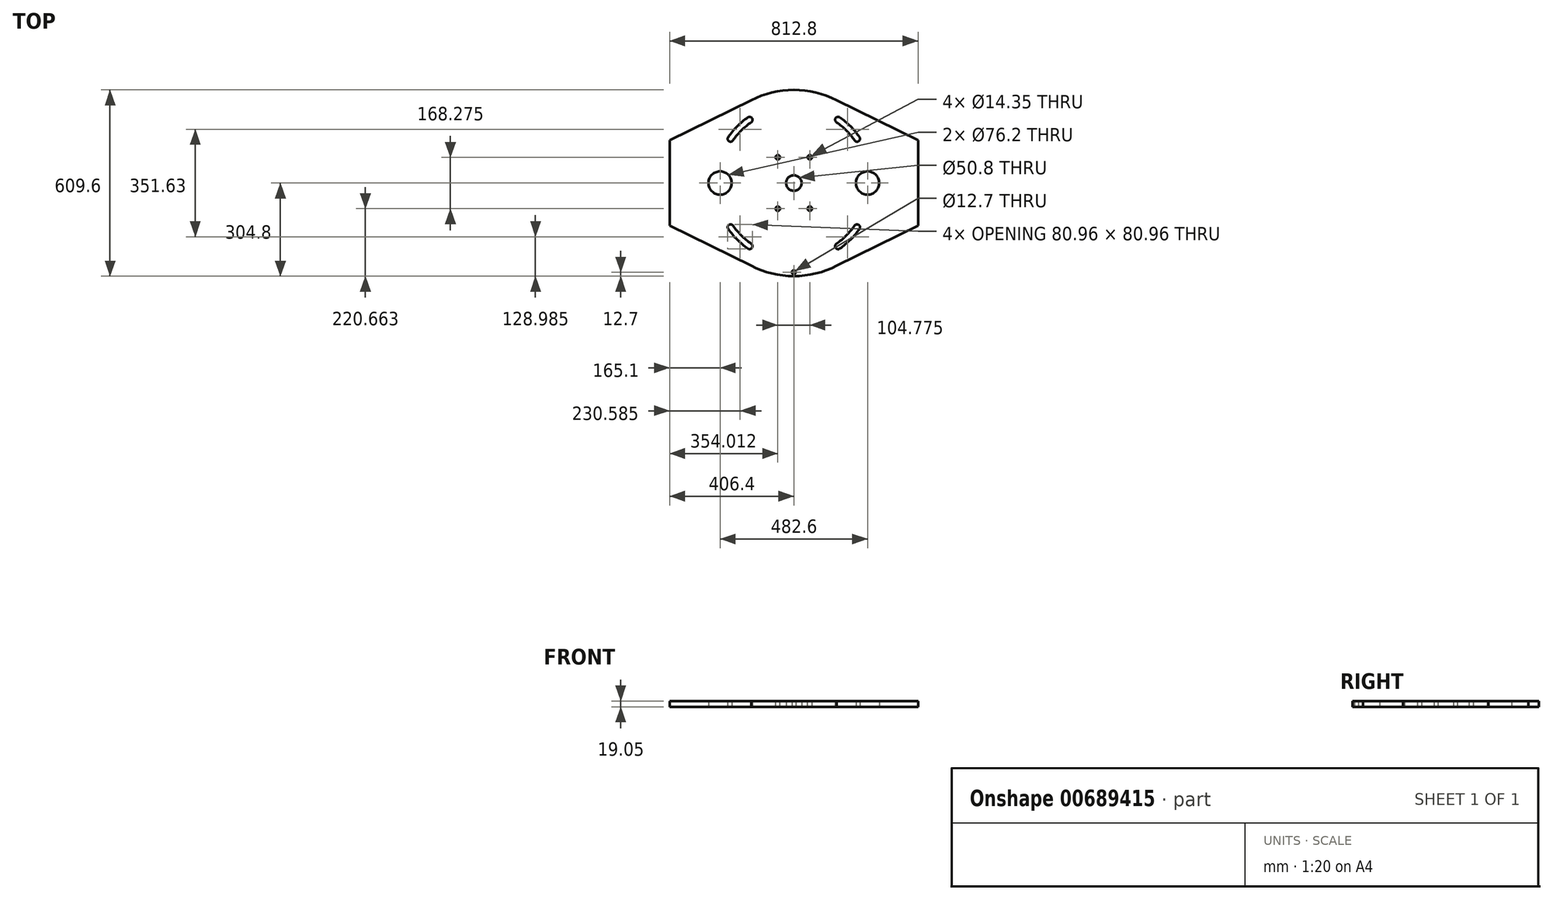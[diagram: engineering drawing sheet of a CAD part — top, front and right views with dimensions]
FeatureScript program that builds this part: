
annotation { "Feature Type Name" : "Feature", "Feature Type Description" : "" }
export const myFeature = defineFeature(function(context is Context, id is Id, definition is map)
    precondition{}
    {
        {
            var Q0;
            Q0=qCreatedBy(makeId("Top.planeOp"),FACE);
            var sketch = newSketch(context, id + "F0", { "sketchPlane" : qUnion([Q0])});
            skCircle(sketch, "E0", {"center": v(0, 0) * mm, "radius": 304.8 * mm});
            skCircle(sketch, "E1", {"center": v(0, 0) * mm, "radius": 25.4 * mm});
            skCircle(sketch, "E2", {"center": v(241.3, 0) * mm, "radius": 38.1 * mm});
            skCircle(sketch, "E3", {"center": v(-241.3, 0) * mm, "radius": 38.1 * mm});
            skArc(sketch, "E4", {"start": v(-198.93, -139.3) * mm, "mid": v(-212.34, -136.93) * mm, "end": v(-214.7, -150.34) * mm});
            skArc(sketch, "E5", {"start": v(-150.34, -214.7) * mm, "mid": v(-136.93, -212.34) * mm, "end": v(-139.3, -198.93) * mm});
            skArc(sketch, "E6", {"start": v(-198.93, -139.3) * mm, "mid": v(-171.72, -171.72) * mm, "end": v(-139.3, -198.93) * mm});
            skArc(sketch, "E7", {"start": v(-214.7, -150.34) * mm, "mid": v(-185.33, -185.33) * mm, "end": v(-150.34, -214.7) * mm});
            skArc(sketch, "E8.1.0", {"start": v(214.7, -150.34) * mm, "mid": v(212.34, -136.93) * mm, "end": v(198.93, -139.3) * mm});
            skArc(sketch, "E8.1.1", {"start": v(139.3, -198.93) * mm, "mid": v(171.72, -171.72) * mm, "end": v(198.93, -139.3) * mm});
            skArc(sketch, "E8.1.2", {"start": v(150.34, -214.7) * mm, "mid": v(185.33, -185.33) * mm, "end": v(214.7, -150.34) * mm});
            skArc(sketch, "E8.1.3", {"start": v(139.3, -198.93) * mm, "mid": v(136.93, -212.34) * mm, "end": v(150.34, -214.7) * mm});
            skArc(sketch, "E8.2.0", {"start": v(150.34, 214.7) * mm, "mid": v(136.93, 212.34) * mm, "end": v(139.3, 198.93) * mm});
            skArc(sketch, "E8.2.1", {"start": v(198.93, 139.3) * mm, "mid": v(171.72, 171.72) * mm, "end": v(139.3, 198.93) * mm});
            skArc(sketch, "E8.2.2", {"start": v(214.7, 150.34) * mm, "mid": v(185.33, 185.33) * mm, "end": v(150.34, 214.7) * mm});
            skArc(sketch, "E8.2.3", {"start": v(198.93, 139.3) * mm, "mid": v(212.34, 136.93) * mm, "end": v(214.7, 150.34) * mm});
            skArc(sketch, "E8.3.0", {"start": v(-214.7, 150.34) * mm, "mid": v(-212.34, 136.93) * mm, "end": v(-198.93, 139.3) * mm});
            skArc(sketch, "E8.3.1", {"start": v(-139.3, 198.93) * mm, "mid": v(-171.72, 171.72) * mm, "end": v(-198.93, 139.3) * mm});
            skArc(sketch, "E8.3.2", {"start": v(-150.34, 214.7) * mm, "mid": v(-185.33, 185.33) * mm, "end": v(-214.7, 150.34) * mm});
            skArc(sketch, "E8.3.3", {"start": v(-139.3, 198.93) * mm, "mid": v(-136.93, 212.34) * mm, "end": v(-150.34, 214.7) * mm});
            skLineSegment(sketch, "E9", {"start": v(-406.4, -139.7) * mm, "end": v(-406.4, 139.7) * mm});
            skLineSegment(sketch, "E10", {"start": v(406.4, -139.7) * mm, "end": v(406.4, 139.7) * mm});
            skPoint(sketch, "E11", {"position": v(139.7, 270.9) * mm});
            skPoint(sketch, "E12", {"position": v(139.7, -270.9) * mm});
            skLineSegment(sketch, "E13", {"start": v(406.4, 139.7) * mm, "end": v(139.7, 270.9) * mm});
            skLineSegment(sketch, "E14", {"start": v(406.4, -139.7) * mm, "end": v(139.7, -270.9) * mm});
            skPoint(sketch, "E15", {"position": v(-139.7, -270.9) * mm});
            skPoint(sketch, "E16", {"position": v(-139.7, 270.9) * mm});
            skLineSegment(sketch, "E17", {"start": v(-406.4, 139.7) * mm, "end": v(-139.7, 270.9) * mm});
            skLineSegment(sketch, "E18", {"start": v(-406.4, -139.7) * mm, "end": v(-139.7, -270.9) * mm});
            skCircle(sketch, "E19", {"center": v(0, -292.1) * mm, "radius": 6.35 * mm});
            skSolve(sketch);
        }
        {
            var Q0;
            Q0=makeQuery(id+"F0.imprint","IMPRINT",FACE,{"disambiguationData":[TD([[makeQuery(id+"F0.imprint","IMPRINT",EDGE,{"derivedFrom":sQuery(id+"F0.wireOp",EDGE,"E1")}),-1.0]])]});
            var Q1;
            Q1=makeQuery(id+"F0.imprint","IMPRINT",FACE,{"disambiguationData":[TD([[makeQuery(id+"F0.imprint","IMPRINT",EDGE,{"derivedFrom":sQuery(id+"F0.wireOp",EDGE,"E9")}),-1.0]])]});
            var Q2;
            Q2=makeQuery(id+"F0.imprint","IMPRINT",FACE,{"disambiguationData":[TD([[makeQuery(id+"F0.imprint","IMPRINT",EDGE,{"derivedFrom":sQuery(id+"F0.wireOp",EDGE,"E10")}),1.0]])]});
            extrude(context, id + "F1", {"entities" : qUnion([Q0, Q1, Q2]), "depth" : 19.05 * mm, "offsetDistance" : 25.4 * mm});
        }
        {
            var Q0;
            Q0=makeQuery(id+"F1.opExtrude","CAP_FACE",FACE,{"disambiguationData":[OSD([sQuery(id+"F0.wireOp",EDGE,"E0"),sQuery(id+"F0.wireOp",EDGE,"E1"),sQuery(id+"F0.wireOp",EDGE,"E2"),sQuery(id+"F0.wireOp",EDGE,"E3"),sQuery(id+"F0.wireOp",EDGE,"E4"),sQuery(id+"F0.wireOp",EDGE,"E5"),sQuery(id+"F0.wireOp",EDGE,"E6"),sQuery(id+"F0.wireOp",EDGE,"E7"),sQuery(id+"F0.wireOp",EDGE,"E8.1.0"),sQuery(id+"F0.wireOp",EDGE,"E8.1.1"),sQuery(id+"F0.wireOp",EDGE,"E8.1.2"),sQuery(id+"F0.wireOp",EDGE,"E8.1.3"),sQuery(id+"F0.wireOp",EDGE,"E8.2.0"),sQuery(id+"F0.wireOp",EDGE,"E8.2.1"),sQuery(id+"F0.wireOp",EDGE,"E8.2.2"),sQuery(id+"F0.wireOp",EDGE,"E8.2.3"),sQuery(id+"F0.wireOp",EDGE,"E8.3.0"),sQuery(id+"F0.wireOp",EDGE,"E8.3.1"),sQuery(id+"F0.wireOp",EDGE,"E8.3.2"),sQuery(id+"F0.wireOp",EDGE,"E8.3.3"),sQuery(id+"F0.wireOp",EDGE,"E9"),sQuery(id+"F0.wireOp",EDGE,"E10"),sQuery(id+"F0.wireOp",EDGE,"E13"),sQuery(id+"F0.wireOp",EDGE,"E14"),sQuery(id+"F0.wireOp",EDGE,"E17"),sQuery(id+"F0.wireOp",EDGE,"E18"),sQuery(id+"F0.wireOp",EDGE,"E19")])],"isStart":false});
            var sketch = newSketch(context, id + "F2", { "sketchPlane" : qUnion([Q0])});
            skPoint(sketch, "E20", {"position": v(52.39, -84.14) * mm});
            skPoint(sketch, "E21", {"position": v(52.39, 84.14) * mm});
            skPoint(sketch, "E22", {"position": v(-52.39, 84.14) * mm});
            skPoint(sketch, "E23", {"position": v(-52.39, -84.14) * mm});
            skSolve(sketch);
        }
        {
            var Q0;
            Q0=sQuery(id+"F2.wireOp",VERTEX,"E22");
            var Q1;
            Q1=sQuery(id+"F2.wireOp",VERTEX,"E23");
            var Q2;
            Q2=sQuery(id+"F2.wireOp",VERTEX,"E20");
            var Q3;
            Q3=sQuery(id+"F2.wireOp",VERTEX,"E21");
            var Q4;
            Q4=makeQuery(id+"F1.opExtrude","SWEPT_BODY",BODY,{"disambiguationData":[OSD([sQuery(id+"F0.wireOp",EDGE,"E0"),sQuery(id+"F0.wireOp",EDGE,"E1"),sQuery(id+"F0.wireOp",EDGE,"E2"),sQuery(id+"F0.wireOp",EDGE,"E3"),sQuery(id+"F0.wireOp",EDGE,"E4"),sQuery(id+"F0.wireOp",EDGE,"E5"),sQuery(id+"F0.wireOp",EDGE,"E6"),sQuery(id+"F0.wireOp",EDGE,"E7"),sQuery(id+"F0.wireOp",EDGE,"E8.1.0"),sQuery(id+"F0.wireOp",EDGE,"E8.1.1"),sQuery(id+"F0.wireOp",EDGE,"E8.1.2"),sQuery(id+"F0.wireOp",EDGE,"E8.1.3"),sQuery(id+"F0.wireOp",EDGE,"E8.2.0"),sQuery(id+"F0.wireOp",EDGE,"E8.2.1"),sQuery(id+"F0.wireOp",EDGE,"E8.2.2"),sQuery(id+"F0.wireOp",EDGE,"E8.2.3"),sQuery(id+"F0.wireOp",EDGE,"E8.3.0"),sQuery(id+"F0.wireOp",EDGE,"E8.3.1"),sQuery(id+"F0.wireOp",EDGE,"E8.3.2"),sQuery(id+"F0.wireOp",EDGE,"E8.3.3"),sQuery(id+"F0.wireOp",EDGE,"E9"),sQuery(id+"F0.wireOp",EDGE,"E10"),sQuery(id+"F0.wireOp",EDGE,"E13"),sQuery(id+"F0.wireOp",EDGE,"E14"),sQuery(id+"F0.wireOp",EDGE,"E17"),sQuery(id+"F0.wireOp",EDGE,"E18"),sQuery(id+"F0.wireOp",EDGE,"E19")])]});
            hole(context, id + "F3", {"style" : HoleStyle.SIMPLE, "endStyle" : HoleEndStyle.THROUGH, "holeDiameter" : 14.35 * mm, "majorDiameter" : 5 * mm, "tappedDepth" : 10.3 * mm, "tapClearance" : 3, "locations" : qUnion([Q0, Q1, Q2, Q3]), "scope" : qUnion([Q4])});
        }
    });
